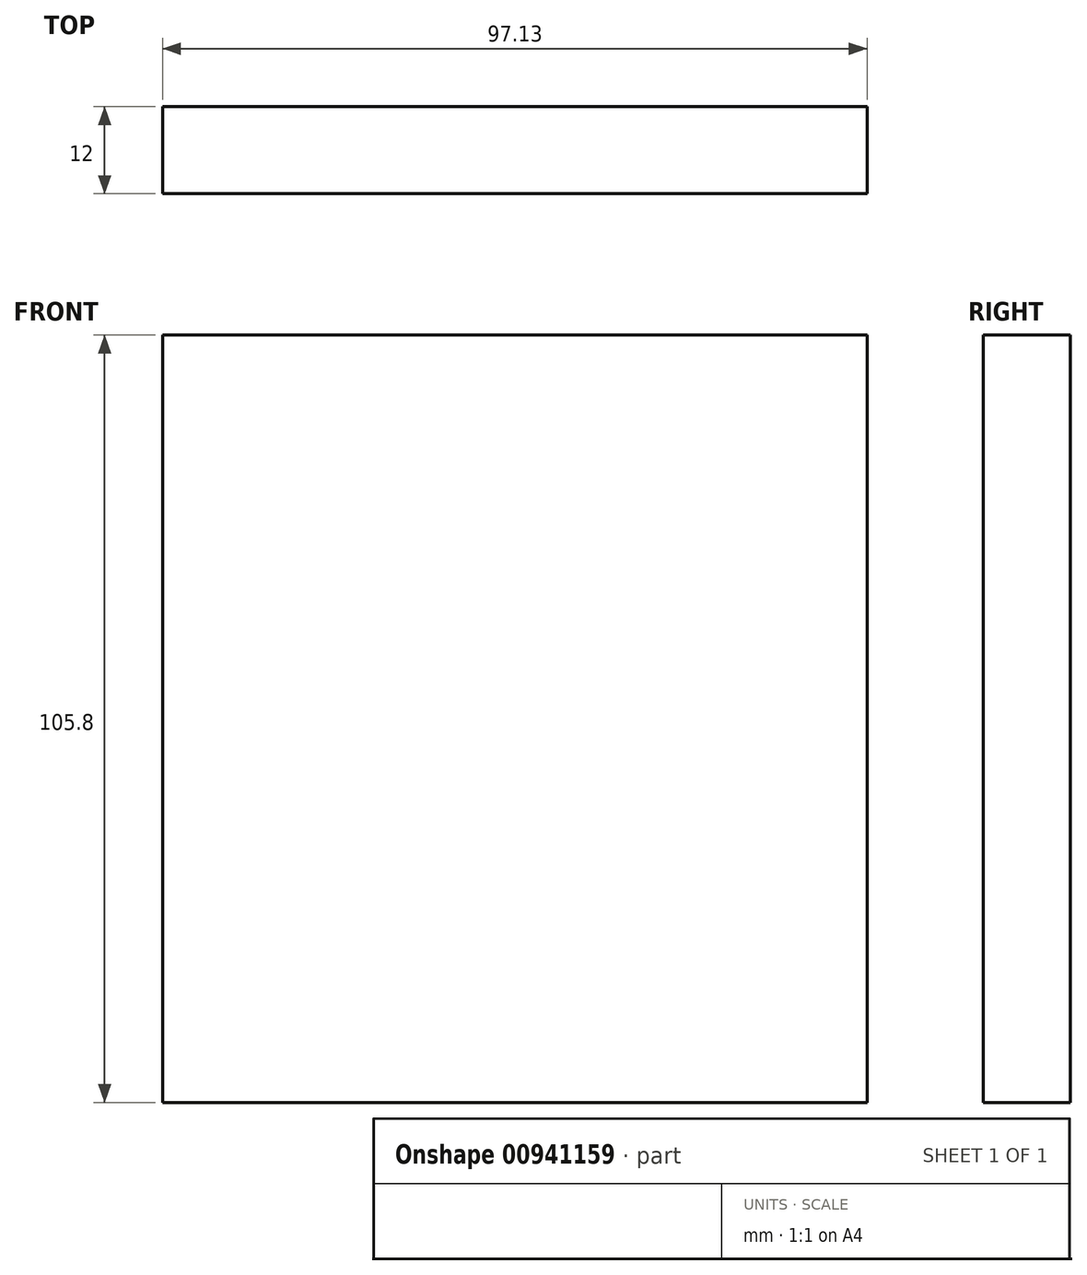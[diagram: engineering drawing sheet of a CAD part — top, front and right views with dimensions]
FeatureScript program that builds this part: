
annotation { "Feature Type Name" : "Feature", "Feature Type Description" : "" }
export const myFeature = defineFeature(function(context is Context, id is Id, definition is map)
    precondition{}
    {
        {
            var Q0;
            Q0=qCreatedBy(makeId("Front.planeOp"),FACE);
            var sketch = newSketch(context, id + "F0", { "sketchPlane" : qUnion([Q0])});
            skLineSegment(sketch, "E0.bottom", {"start": v(-52.32, 47.76) * mm, "end": v(44.8, 47.76) * mm});
            skLineSegment(sketch, "E0.top", {"start": v(-52.32, -58.04) * mm, "end": v(44.8, -58.04) * mm});
            skLineSegment(sketch, "E0.left", {"start": v(-52.32, 47.76) * mm, "end": v(-52.32, -58.04) * mm});
            skLineSegment(sketch, "E0.right", {"start": v(44.8, 47.76) * mm, "end": v(44.8, -58.04) * mm});
            skSolve(sketch);
        }
        {
            var Q0;
            Q0 = qSketchRegion(id + "F0", true);
            extrude(context, id + "F1", {"entities" : qUnion([Q0]), "depth" : 12 * mm, "offsetDistance" : 25 * mm});
        }
    });
